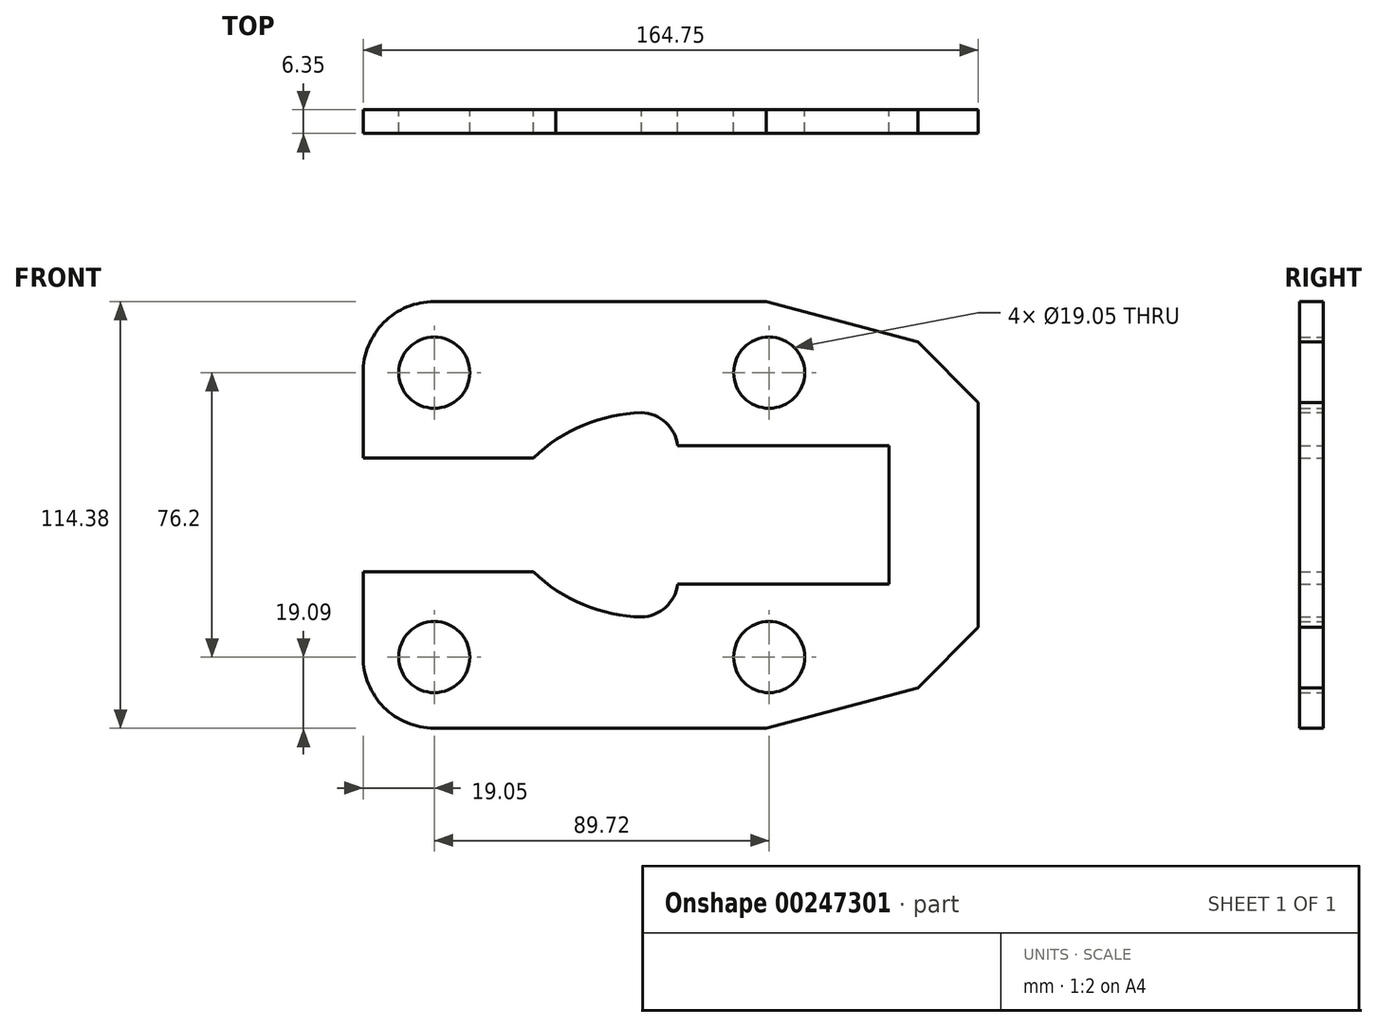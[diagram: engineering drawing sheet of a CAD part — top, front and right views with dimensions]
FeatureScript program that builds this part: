
annotation { "Feature Type Name" : "Feature", "Feature Type Description" : "" }
export const myFeature = defineFeature(function(context is Context, id is Id, definition is map)
    precondition{}
    {
        {
            var Q0;
            Q0=qCreatedBy(makeId("Front.planeOp"),FACE);
            var sketch = newSketch(context, id + "F0", { "sketchPlane" : qUnion([Q0])});
            skLineSegment(sketch, "E0.top", {"start": v(0.85, 15.24) * mm, "end": v(45.61, 15.24) * mm});
            skArc(sketch, "E1", {"start": v(19.04, 57.15) * mm, "mid": v(5.53, 51.52) * mm, "end": v(0, 37.97) * mm});
            skCircle(sketch, "E2", {"center": v(19.05, 38.1) * mm, "radius": 9.53 * mm});
            skLineSegment(sketch, "E3", {"start": v(19.04, 57.15) * mm, "end": v(107.94, 57.19) * mm});
            skPoint(sketch, "E0.bottom.start.orphan", {"position": v(0, 0) * mm});
            skLineSegment(sketch, "E4.bottom", {"start": v(107.94, 57.19) * mm, "end": v(51.65, 57.19) * mm});
            skLineSegment(sketch, "E4.right", {"start": v(51.65, 57.19) * mm, "end": v(51.65, 57.16) * mm});
            skLineSegment(sketch, "E5", {"start": v(0, 38.1) * mm, "end": v(0.08, 15.24) * mm});
            skPoint(sketch, "E6.orphan", {"position": v(0.08, 36.36) * mm});
            skLineSegment(sketch, "E7", {"start": v(0.85, 15.24) * mm, "end": v(0.08, 15.24) * mm});
            skPoint(sketch, "E8.orphan", {"position": v(0.08, 14.26) * mm});
            skLineSegment(sketch, "E9", {"start": v(107.94, 57.19) * mm, "end": v(148.58, 46.3) * mm});
            skLineSegment(sketch, "E10", {"start": v(148.58, 46.3) * mm, "end": v(164.75, 30.14) * mm});
            skPoint(sketch, "E11.orphan", {"position": v(160.01, 57.19) * mm});
            skPoint(sketch, "E12.bottom.end.orphan", {"position": v(148.58, 57.19) * mm});
            skArc(sketch, "E13", {"start": v(84.3, 18.53) * mm, "mid": v(81.07, 24.72) * mm, "end": v(74.6, 27.37) * mm});
            skLineSegment(sketch, "E14", {"start": v(84.3, 18.53) * mm, "end": v(140.87, 18.53) * mm});
            skPoint(sketch, "E15.top.end.orphan", {"position": v(136.14, -5.17) * mm});
            skLineSegment(sketch, "E16.right", {"start": v(140.87, 18.53) * mm, "end": v(140.87, -1.8) * mm});
            skArc(sketch, "E17", {"start": v(74.6, 27.37) * mm, "mid": v(58.97, 24.02) * mm, "end": v(45.61, 15.24) * mm});
            skPoint(sketch, "E18.orphan", {"position": v(51.65, 15.24) * mm});
            skCircle(sketch, "E19", {"center": v(108.77, 38.1) * mm, "radius": 9.53 * mm});
            skLineSegment(sketch, "E20.MirrorCS", {"start": v(0.85, -15.24) * mm, "end": v(45.61, -15.24) * mm});
            skArc(sketch, "E21.MirrorCS", {"start": v(74.6, -27.37) * mm, "mid": v(58.97, -24.02) * mm, "end": v(45.61, -15.24) * mm});
            skArc(sketch, "E22.MirrorCS", {"start": v(84.3, -18.53) * mm, "mid": v(81.07, -24.72) * mm, "end": v(74.6, -27.37) * mm});
            skLineSegment(sketch, "E23.MirrorCS", {"start": v(84.3, -18.53) * mm, "end": v(140.87, -18.53) * mm});
            skLineSegment(sketch, "E24.MirrorCS", {"start": v(140.87, -18.53) * mm, "end": v(140.87, 1.8) * mm});
            skLineSegment(sketch, "E25.MirrorCS", {"start": v(148.58, -46.3) * mm, "end": v(164.75, -30.14) * mm});
            skLineSegment(sketch, "E26.MirrorCS", {"start": v(107.94, -57.19) * mm, "end": v(148.58, -46.3) * mm});
            skLineSegment(sketch, "E27.MirrorCS", {"start": v(107.94, -57.19) * mm, "end": v(51.65, -57.19) * mm});
            skLineSegment(sketch, "E28.MirrorCS", {"start": v(19.04, -57.15) * mm, "end": v(107.94, -57.19) * mm});
            skArc(sketch, "E29.MirrorCS", {"start": v(19.04, -57.15) * mm, "mid": v(5.53, -51.52) * mm, "end": v(0, -37.97) * mm});
            skLineSegment(sketch, "E30.MirrorCS", {"start": v(0, -38.1) * mm, "end": v(0.08, -15.24) * mm});
            skCircle(sketch, "E31.MirrorC", {"center": v(108.77, -38.1) * mm, "radius": 9.53 * mm});
            skCircle(sketch, "E32.MirrorC", {"center": v(19.05, -38.1) * mm, "radius": 9.53 * mm});
            skPoint(sketch, "E33.MirrorCS.end.orphan", {"position": v(140.87, 1.8) * mm});
            skLineSegment(sketch, "E34", {"start": v(0.85, -15.24) * mm, "end": v(0.08, -15.24) * mm});
            skLineSegment(sketch, "E35", {"start": v(164.75, 1.84) * mm, "end": v(164.75, 30.14) * mm});
            skPoint(sketch, "E36.MirrorCS.start.orphan", {"position": v(164.75, -30.14) * mm});
            skLineSegment(sketch, "E37", {"start": v(164.75, 1.84) * mm, "end": v(164.75, -30.14) * mm});
            skSolve(sketch);
        }
        {
            var Q0;
            Q0 = qSketchRegion(id + "F0", true);
            extrude(context, id + "F1", {"entities" : qUnion([Q0]), "depth" : 6.35 * mm});
        }
    });
